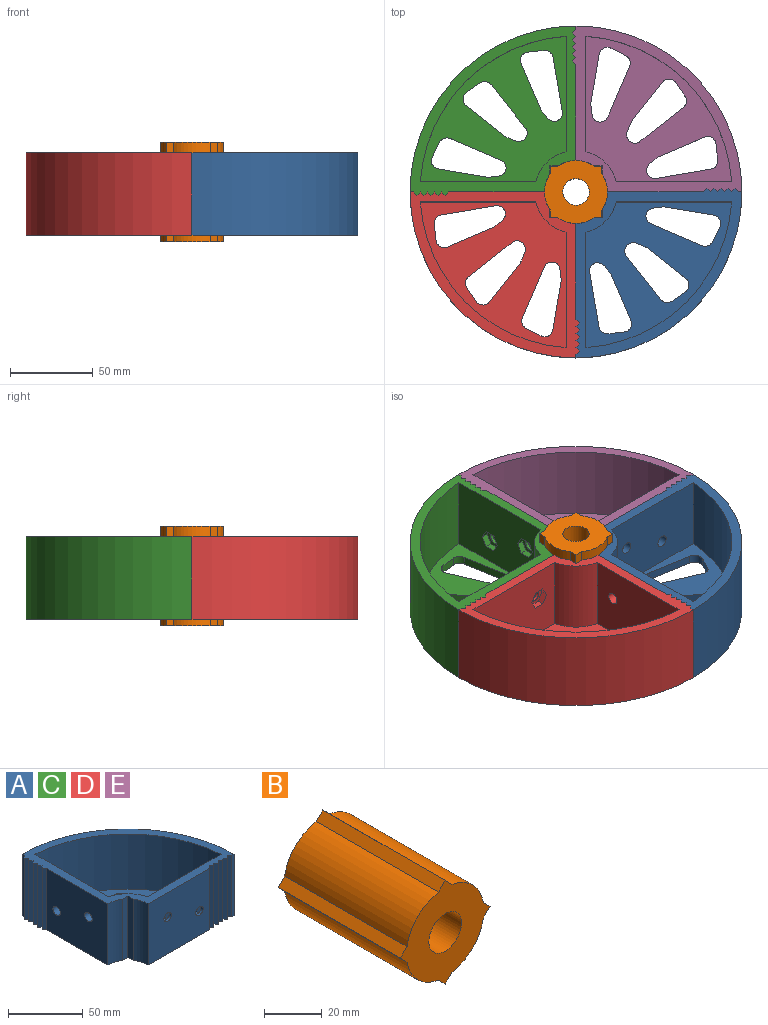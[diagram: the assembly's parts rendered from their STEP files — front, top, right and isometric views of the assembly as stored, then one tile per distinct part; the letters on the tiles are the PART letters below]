
ASSEMBLY  parts=5 mates=9
PART A: 78 faces, bbox 102.1x100x50 mm
  f0: plane 102.12x100mm, normal (0,0,1), area 1940.8mm2, adj f1,f3,f4,f6,f7,f8,f9,f10
  f1: cylinder r=19mm len=50mm, axis (0,0,1), area 568.5mm2, adj f0,f2,f9,f76
  f2: plane 102.12x100mm, normal (0,0,-1), area 5583mm2, adj f1,f6,f7,f8,f9,f10,f12,f13
  f3: plane 69.54x45mm, normal (0,1,0), area 2919.7mm2, adj f0,f5,f11,f32,f33,f34,f35,f36
  f4: plane 69.54x45mm, normal (1,0,0), area 3052.3mm2, adj f0,f5,f11,f72,f74,f75
  f5: plane 87.81x87.81mm, normal (0,0,1), area 3642.2mm2, adj f3,f4,f11,f48,f49,f50,f51,f52
  f6: plane 50x2mm, normal (-1,0,0), area 100mm2, adj f0,f2,f10,f31
  f7: plane 50x2mm, normal (0,-1,0), area 100mm2, adj f0,f2,f10,f21
  f8: plane 57.79x50mm, normal (-1,0,0), area 2812.4mm2, adj f0,f2,f30,f73,f74,f75
  f9: plane 57.79x50mm, normal (0,-1,0), area 2812.4mm2, adj f0,f1,f2,f20,f46,f47
  f10: cylinder r=100mm len=100mm, axis (0,0,-1), area 7854mm2, adj f0,f2,f6,f7
  f11: cylinder r=94mm len=87.81mm, axis (0,0,1), area 6104.1mm2, adj f0,f3,f4,f5
  f12: plane 50x2.12mm, normal (0.71,-0.71,0), area 150mm2, adj f0,f2,f13,f21
  f13: plane 50x2.12mm, normal (-0.71,-0.71,0), area 150mm2, adj f0,f2,f12,f14
  f14: plane 50x2.12mm, normal (0.71,-0.71,0), area 150mm2, adj f0,f2,f13,f15
  f15: plane 50x2.12mm, normal (-0.71,-0.71,0), area 150mm2, adj f0,f2,f14,f16
  f16: plane 50x2.12mm, normal (0.71,-0.71,0), area 150mm2, adj f0,f2,f15,f17
  f17: plane 50x2.12mm, normal (-0.71,-0.71,0), area 150mm2, adj f0,f2,f16,f18
  f18: plane 50x2.12mm, normal (0.71,-0.71,0), area 150mm2, adj f0,f2,f17,f19
  f19: plane 50x2.12mm, normal (-0.71,-0.71,0), area 150mm2, adj f0,f2,f18,f20
  f20: plane 50x2.12mm, normal (0.71,-0.71,0), area 150mm2, adj f0,f2,f9,f19
  f21: plane 50x2.12mm, normal (-0.71,-0.71,0), area 150mm2, adj f0,f2,f7,f12
  f22: plane 50x2.12mm, normal (-0.71,-0.71,0), area 150mm2, adj f0,f2,f23,f31
  f23: plane 50x2.12mm, normal (-0.71,0.71,0), area 150mm2, adj f0,f2,f22,f24
  f24: plane 50x2.12mm, normal (-0.71,-0.71,0), area 150mm2, adj f0,f2,f23,f25
  f25: plane 50x2.12mm, normal (-0.71,0.71,0), area 150mm2, adj f0,f2,f24,f26
  f26: plane 50x2.12mm, normal (-0.71,-0.71,0), area 150mm2, adj f0,f2,f25,f27
  f27: plane 50x2.12mm, normal (-0.71,0.71,0), area 150mm2, adj f0,f2,f26,f28
  f28: plane 50x2.12mm, normal (-0.71,-0.71,0), area 150mm2, adj f0,f2,f27,f29
  f29: plane 50x2.12mm, normal (-0.71,0.71,0), area 150mm2, adj f0,f2,f28,f30
  f30: plane 50x2.12mm, normal (-0.71,-0.71,0), area 150mm2, adj f0,f2,f8,f29
  f31: plane 50x2.12mm, normal (-0.71,0.71,0), area 150mm2, adj f0,f2,f6,f22
  f32: plane 6.35x4mm, normal (0,0,-1), area 25.4mm2, adj f3,f33,f37,f38
  f33: plane 5.5x4mm, normal (-0.87,0,-0.5), area 25.4mm2, adj f3,f32,f34,f38
  f34: plane 5.5x4mm, normal (-0.87,0,0.5), area 25.4mm2, adj f3,f33,f35,f38
  f35: plane 6.35x4mm, normal (0,0,1), area 25.4mm2, adj f3,f34,f36,f38
  f36: plane 5.5x4mm, normal (0.87,0,0.5), area 25.4mm2, adj f3,f35,f37,f38
  f37: plane 5.5x4mm, normal (0.87,0,-0.5), area 25.4mm2, adj f3,f32,f36,f38
  f38: plane 12.7x11mm, normal (0,1,0), area 66.3mm2, adj f32,f33,f34,f35,f36,f37,f47
  f39: plane 6.35x4mm, normal (0,0,-1), area 25.4mm2, adj f3,f40,f44,f45
  f40: plane 5.5x4mm, normal (-0.87,0,-0.5), area 25.4mm2, adj f3,f39,f41,f45
  f41: plane 5.5x4mm, normal (-0.87,0,0.5), area 25.4mm2, adj f3,f40,f42,f45
  f42: plane 6.35x4mm, normal (0,0,1), area 25.4mm2, adj f3,f41,f43,f45
  f43: plane 5.5x4mm, normal (0.87,0,0.5), area 25.4mm2, adj f3,f42,f44,f45
  f44: plane 5.5x4mm, normal (0.87,0,-0.5), area 25.4mm2, adj f3,f39,f43,f45
  f45: plane 12.7x11mm, normal (0,1,0), area 66.3mm2, adj f39,f40,f41,f42,f43,f44,f46
  f46: cylinder r=3.5mm len=7mm, axis (0,1,0), area 44mm2, adj f9,f45
  f47: cylinder r=3.5mm len=7mm, axis (0,1,0), area 44mm2, adj f9,f38
  f48: plane 8.79x5mm, normal (-0.45,-0.89,0), area 49.1mm2, adj f2,f5,f68,f71
  f49: plane 29.3x5mm, normal (0.99,-0.17,0), area 148.6mm2, adj f2,f5,f70,f71
  f50: plane 5.73x5mm, normal (0.99,0.12,0), area 28.8mm2, adj f2,f5,f69,f70
  f51: plane 30.63x13.02mm, normal (-0.92,0.39,0), area 166.4mm2, adj f2,f5,f68,f69
  f52: plane 32.82x5.58mm, normal (-0.17,0.99,0), area 166.4mm2, adj f2,f5,f61,f63
  f53: plane 9.77x5mm, normal (-0.99,-0.11,0), area 49.1mm2, adj f2,f5,f60,f61
  f54: plane 27.32x11.69mm, normal (0.39,-0.92,0), area 148.6mm2, adj f2,f5,f60,f62
  f55: plane 5x4.45mm, normal (0.64,-0.77,0), area 28.8mm2, adj f2,f5,f62,f63
  f56: plane 23.36x18.37mm, normal (0.79,-0.62,0), area 148.6mm2, adj f2,f5,f64,f67
  f57: plane 5.35x5mm, normal (0.93,-0.37,0), area 28.8mm2, adj f2,f5,f64,f65
  f58: plane 26.12x20.63mm, normal (-0.62,0.78,0), area 166.4mm2, adj f2,f5,f65,f66
  f59: plane 8.07x5.61mm, normal (-0.82,-0.57,0), area 49.1mm2, adj f2,f5,f66,f67
  f60: cylinder r=5mm len=6.94mm, axis (0,0,1), area 46.7mm2, adj f2,f5,f53,f54
  f61: cylinder r=5mm len=5.46mm, axis (0,0,1), area 37.7mm2, adj f2,f5,f52,f53
  f62: cylinder r=5mm len=5mm, axis (0,0,1), area 7.1mm2, adj f2,f5,f54,f55
  f63: cylinder r=5mm len=8.86mm, axis (0,0,1), area 65.5mm2, adj f2,f5,f52,f55
  f64: cylinder r=5mm len=5mm, axis (0,0,1), area 7.1mm2, adj f2,f5,f56,f57
  f65: cylinder r=5mm len=8.1mm, axis (0,0,1), area 65.5mm2, adj f2,f5,f57,f58
  f66: cylinder r=5mm len=6.78mm, axis (0,0,1), area 37.7mm2, adj f2,f5,f58,f59
  f67: cylinder r=5mm len=8.04mm, axis (0,0,1), area 46.7mm2, adj f2,f5,f56,f59
  f68: cylinder r=5mm len=6.43mm, axis (0,0,-1), area 37.7mm2, adj f2,f5,f48,f51
  f69: cylinder r=5mm len=9.57mm, axis (0,0,-1), area 65.5mm2, adj f2,f5,f50,f51
  f70: cylinder r=5mm len=5mm, axis (0,0,-1), area 7.1mm2, adj f2,f5,f49,f50
  f71: cylinder r=5mm len=7.17mm, axis (0,0,-1), area 46.7mm2, adj f2,f5,f48,f49
  f72: cylinder r=25mm len=45mm, axis (0,0,1), area 1221.8mm2, adj f0,f3,f4,f5
  f73: cylinder r=19mm len=50mm, axis (0,0,1), area 568.5mm2, adj f0,f2,f8,f77
  f74: cylinder r=3.5mm len=7mm, axis (1,0,0), area 131.9mm2, adj f4,f8
  f75: cylinder r=3.5mm len=7mm, axis (1,0,0), area 131.9mm2, adj f4,f8
  f76: plane 50x4.99mm, normal (-1,0,0), area 249.7mm2, adj f0,f1,f2,f77
  f77: plane 50x4.99mm, normal (0,-1,0), area 249.7mm2, adj f0,f2,f73,f76
PART B: 15 faces, bbox 44x60x44 mm
  f0: plane 60x3.29mm, normal (0.71,0,0.71), area 278.9mm2, adj f1,f11,f13,f14
  f1: cylinder r=19mm len=60mm, axis (0,1,0), area 1394.3mm2, adj f0,f2,f13,f14
  f2: plane 60x3.29mm, normal (0.71,0,0.71), area 278.9mm2, adj f1,f3,f13,f14
  f3: plane 60x3.29mm, normal (-0.71,0,0.71), area 278.9mm2, adj f2,f4,f13,f14
  f4: cylinder r=19mm len=60mm, axis (0,1,0), area 1394.3mm2, adj f3,f5,f13,f14
  f5: plane 60x3.29mm, normal (-0.71,0,0.71), area 278.9mm2, adj f4,f6,f13,f14
  f6: plane 60x3.29mm, normal (-0.71,0,-0.71), area 278.9mm2, adj f5,f7,f13,f14
  f7: cylinder r=19mm len=60mm, axis (0,1,0), area 1394.3mm2, adj f6,f8,f13,f14
  f8: plane 60x3.29mm, normal (-0.71,0,-0.71), area 278.9mm2, adj f7,f9,f13,f14
  f9: plane 60x3.29mm, normal (0.71,0,-0.71), area 278.9mm2, adj f8,f10,f13,f14
  f10: cylinder r=19mm len=60mm, axis (0,1,0), area 1394.3mm2, adj f9,f11,f13,f14
  f11: plane 60x3.29mm, normal (0.71,0,-0.71), area 278.9mm2, adj f0,f10,f13,f14
  f12: cylinder r=8mm len=60mm, axis (0,1,0), area 3015.9mm2, adj f13,f14
  f13: plane 44x44mm, normal (0,-1,0), area 971.2mm2, adj f0,f1,f2,f3,f4,f5,f6,f7
  f14: plane 44x44mm, normal (0,1,0), area 971.2mm2, adj f0,f1,f2,f3,f4,f5,f6,f7
PART C: same geometry as A
PART D: same geometry as A
PART E: same geometry as A
PLACE A rot(axis=(0,0,-1),90deg) t=(81.15,-143.95,43.23)mm
PLACE B rot(axis=(-0.28,-0.68,0.68),148.6deg) t=(81.15,-143.95,39.43)mm
PLACE C rot(axis=(0,0,1),90deg) t=(81.15,-143.95,43.23)mm
PLACE D rot(axis=(0,0,1),180deg) t=(81.15,-143.95,43.23)mm
PLACE E t=(81.15,-143.95,43.23)mm
MATE planar D.f0 <-> A.f0  axis (0,0,1) through (81.15,-220.74,93.23)mm
MATE cylindrical D.f1 <-> A.f1  axis (0,0,-1) through (81.15,-143.95,43.23)mm
MATE cylindrical D.f10 <-> E.f1  axis (0,0,-1) through (81.15,-143.95,43.23)mm
MATE cylindrical B.f12 <-> A.f10  axis (0,0,-1) through (81.15,-143.95,39.43)mm
MATE planar A.f8 <-> E.f9  axis (0,1,0) through (128.92,-143.95,68.23)mm
MATE planar C.f0 <-> E.f0  axis (0,0,1) through (75.15,-84.91,93.23)mm
MATE planar D.f9 <-> C.f8  axis (0,1,0) through (33.37,-143.95,68.23)mm
MATE planar A.f0 <-> E.f0  axis (0,0,1) through (129.04,-143.95,93.23)mm
MATE planar C.f9 <-> E.f8  axis (1,0,0) through (81.15,-96.06,43.23)mm
